# Revit family: Rotor 5000 Series - 5004+PCSAMRNP
name_source: partatom
category: Acessórios do tubo
units: mm (PartAtom-declared; Revit-internal decimal feet)

## family parameters
Com base no plano de trabalho = Não
Compartilhado = Não
Corte com vazios quando carregada = Não
Cota do conector redondo = Utilizar diâmetro
Número OmniClass = 23.60.30.11.14
Sempre na vertical = Sim
Tipo de parte = Normal
Título OmniClass = Pipework Fittings

## types (24) — shared parameters
Angle = 25.00°
Black Plastic = Black Plastic
Blue = Blue Plastic
Body height = 1 '
Descrição = 5004+PC-SAM-R-NP Rotor
Fabricante = Rain Bird
Modelo = 5004+PCSAMRNP
RainBird: Code = Y65670NP
RainBird: Description = 5004+PC-SAM-R-NP Rotor
RainBird: Product Link = https://www.rainbird.com
Side inlet = Não
SupportProjetos: Level of Detail = LOD 300
SupportProjetos: Reviw = R00
TABLE 25 = TABLE 25psi
TABLE 35 = TABLE 35psi
TABLE 45 = TABLE 45psi
TABLE 55 = TABLE 55psi
TABLE 55 75 = TABLE 55 75psi
TABLE 65 = TABLE 65psi
URL = https://www.rainbird.com
Water = Water
zero-valued in all types: Conection, DD1, DD10, DD11, DD12, DD13, DD3, DD4, DD5, DD7, Elevação padrão, H1, Pop up height, R1, R2, R3, R4, R5, RN, RT

## per-type parameters (varying)
| type | Instance |
| Rain Curtain 1.5 | 1 ' |
| Rain Curtain 2.0 | 2 ' |
| Rain Curtain 3.0 | 4 ' |
| Rain Curtain 4.0 | 5 ' |
| Rain Curtain 5.0 | 6 ' |
| Rain Curtain 6.0 | 7 ' |
| Rain Curtain 8.0 | 8 ' |
| Rain Curtain 2.5 | 3 ' |
| 1.0 LA | 9 ' |
| 1.5 LA | 10 ' |
| 2.0 LA | 11 ' |
| 3.0 LA | 12 ' |
| PRS Rain Curtain 1.5 | 13 ' |
| PRS Rain Curtain 2.0 | 14 ' |
| PRS Rain Curtain 2.5 | 15 ' |
| PRS Rain Curtain 3.0 | 16 ' |
| PRS Rain Curtain 4.0 | 17 ' |
| PRS Rain Curtain 5.0 | 18 ' |
| PRS Rain Curtain 6.0 | 19 ' |
| PRS Rain Curtain 8.0 | 20 ' |
| PRS 1.0 LA | 21 ' |
| PRS 1.5 LA | 22 ' |
| PRS 2.0 LA | 23 ' |
| PRS 3.0 LA | 24 ' |
